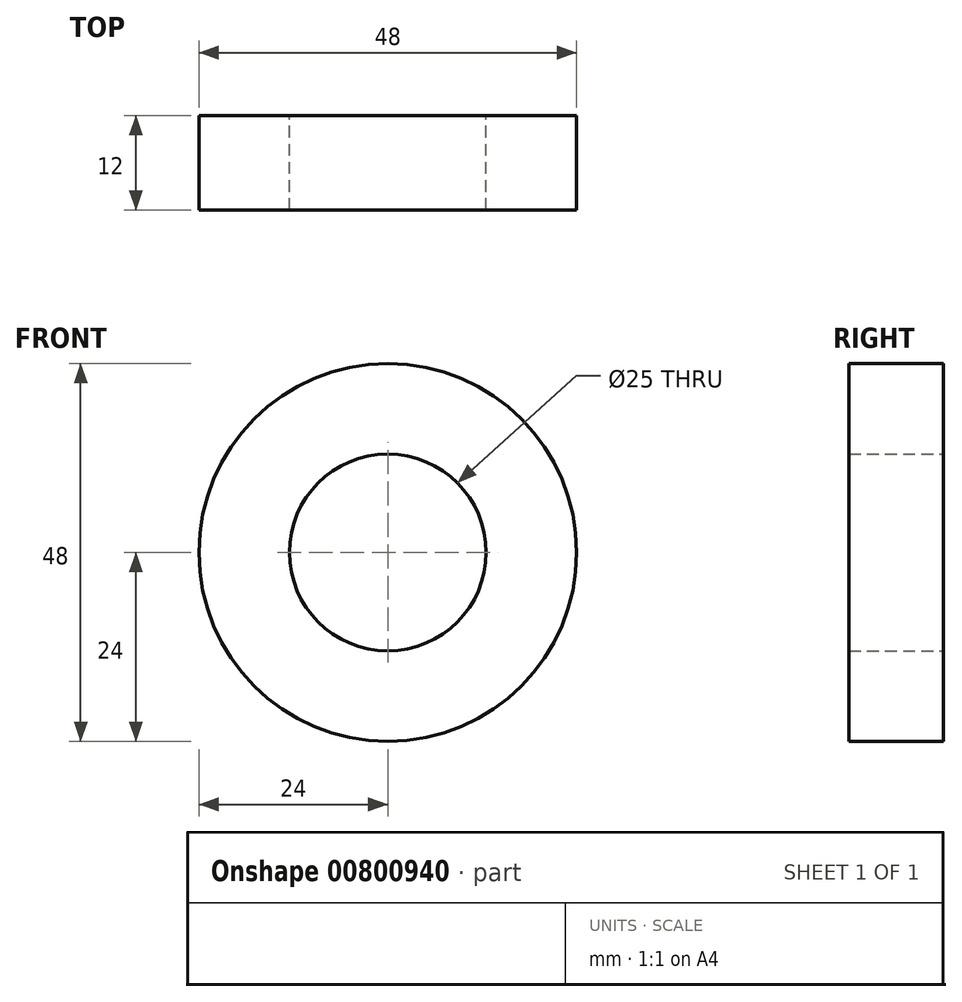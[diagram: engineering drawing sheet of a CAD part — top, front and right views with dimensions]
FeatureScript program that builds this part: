
annotation { "Feature Type Name" : "Feature", "Feature Type Description" : "" }
export const myFeature = defineFeature(function(context is Context, id is Id, definition is map)
    precondition{}
    {
        {
            var Q0;
            Q0=qCreatedBy(makeId("Front.planeOp"),FACE);
            var sketch = newSketch(context, id + "F0", { "sketchPlane" : qUnion([Q0])});
            skCircle(sketch, "E0", {"center": v(0, 0) * mm, "radius": 24 * mm});
            skCircle(sketch, "E1", {"center": v(0, 0) * mm, "radius": 12.5 * mm});
            skSolve(sketch);
        }
        {
            var Q0;
            Q0 = qSketchRegion(id + "F0", true);
            extrude(context, id + "F1", {"entities" : qUnion([Q0]), "depth" : 12 * mm, "offsetDistance" : 25 * mm});
        }
    });
